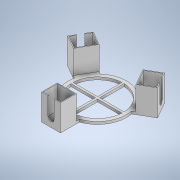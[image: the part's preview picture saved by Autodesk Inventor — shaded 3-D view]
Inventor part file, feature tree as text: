
AUTODESK INVENTOR PART (.ipt)
format: ipt  version: 2020 (Build 240168000, 168)  size: 218,624 bytes
history: native  units: mm
features: extrude x3, sketch x3, pattern_circular x1
ambient origin geometry x8: Origin, YZ Plane, XZ Plane, XY Plane, X Axis, Y Axis, Z Axis, Center Point
bodies: Solid1 (feature_tree)
feature tree (7):
  extrude  "Extrusion1"  Depth=100.0mm
  extrude  "Extrusion2"  Depth=4.0mm
  extrude  "Extrusion3"  Depth=46.0mm
  pattern_circular  "Circular Pattern1"  [2 undecoded]
  sketch  "Sketch1"  dims[d0=114.0mm d1=100.0mm]
  sketch  "Sketch2"  dims[d6=100.0mm d7=4.0mm]
  sketch  "Sketch4"  dims[d8=4.0mm d9=100.0mm d10=37.0mm d14=60.0mm d15=31.0mm d16=30.0mm d18=360.0deg d20=5.0mm d21=0.0mm d22=31.0mm d23=1.5mm d24=30.0mm d26=360.0deg d28=46.0mm d29=0.0mm d30=30.0mm d31=360.0deg d36=12.0mm d37=5.0mm d38=6.0mm d39=46.0mm d40=0.0mm]
note: 2 required parameter values undecoded (feature->parameter linkage not recoverable at this tier; creation-order binding heuristic only, values carry confidence <= 0.55)
